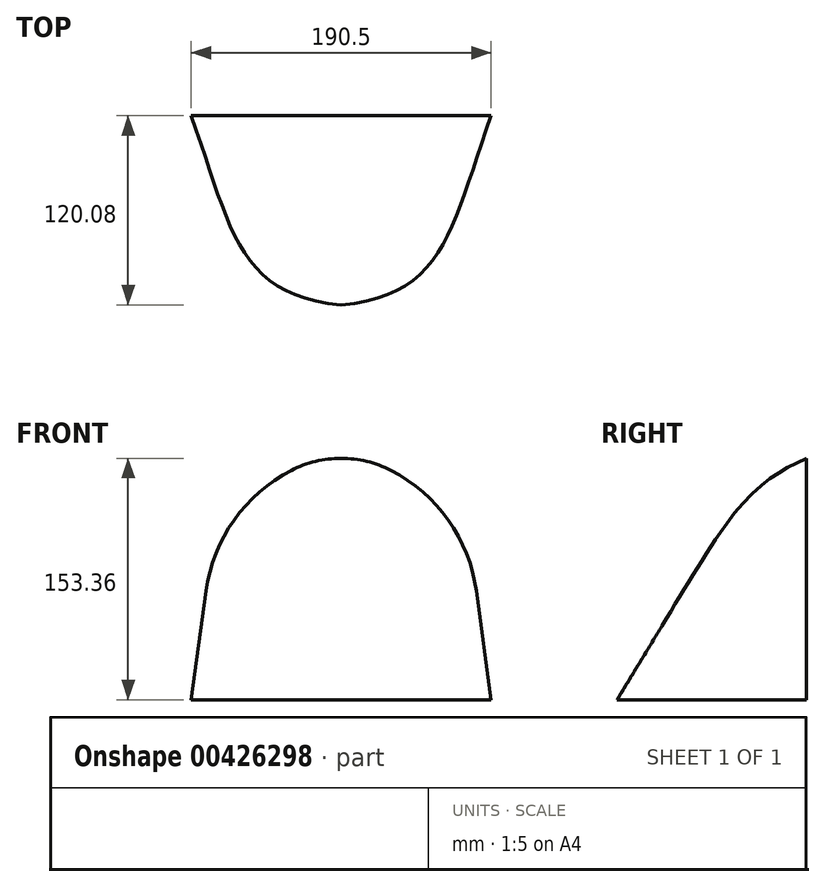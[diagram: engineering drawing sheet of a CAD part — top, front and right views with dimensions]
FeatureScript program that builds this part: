
annotation { "Feature Type Name" : "Feature", "Feature Type Description" : "" }
export const myFeature = defineFeature(function(context is Context, id is Id, definition is map)
    precondition{}
    {
        {
            var Q0;
            Q0=qCreatedBy(makeId("Front.planeOp"),FACE);
            var sketch = newSketch(context, id + "F0", { "sketchPlane" : qUnion([Q0])});
            skLineSegment(sketch, "E0", {"start": v(0, 111.3) * mm, "end": v(0, 0) * mm, "construction": true});
            skLineSegment(sketch, "E1", {"start": v(0, 0) * mm, "end": v(95.25, 0) * mm});
            skLineSegment(sketch, "E2", {"start": v(95.25, 0) * mm, "end": v(85.8, 69.13) * mm});
            skArc(sketch, "E3", {"start": v(85.8, 69.13) * mm, "mid": v(68.09, 114.03) * mm, "end": v(31.65, 145.7) * mm});
            skArc(sketch, "E4", {"start": v(31.65, 145.7) * mm, "mid": v(0, 153.36) * mm, "end": v(-31.65, 145.7) * mm});
            skArc(sketch, "E5.MirrorCS", {"start": v(-85.8, 69.13) * mm, "mid": v(-68.09, 114.03) * mm, "end": v(-31.65, 145.7) * mm});
            skLineSegment(sketch, "E6.MirrorCS", {"start": v(-95.25, 0) * mm, "end": v(-85.8, 69.13) * mm});
            skLineSegment(sketch, "E7.MirrorCS", {"start": v(0, 0) * mm, "end": v(-95.25, 0) * mm});
            skSolve(sketch);
        }
        {
            var Q0;
            Q0=qCreatedBy(makeId("Top.planeOp"),FACE);
            var sketch = newSketch(context, id + "F1", { "sketchPlane" : qUnion([Q0])});
            skLineSegment(sketch, "E8", {"start": v(-95.25, 0) * mm, "end": v(-70.05, -70.7) * mm, "construction": true});
            skArc(sketch, "E9", {"start": v(-70.05, -70.7) * mm, "mid": v(0, -120.08) * mm, "end": v(70.05, -70.7) * mm, "construction": true});
            skLineSegment(sketch, "E10", {"start": v(0, -4.05) * mm, "end": v(0, -115.34) * mm, "construction": true});
            skLineSegment(sketch, "E11", {"start": v(-95.25, 0) * mm, "end": v(95.25, 0) * mm});
            skLineSegment(sketch, "E12.MirrorCS", {"start": v(95.25, 0) * mm, "end": v(70.05, -70.7) * mm, "construction": true});
            skFitSpline(sketch, "E13", {"points": [v(0, -120.08) * mm, v(-95.25, 0) * mm], "startDerivative": vector(-198.66, 17.48) * mm, "endDerivative": vector(-75.61, 212.08) * mm});
            skFitSpline(sketch, "E14.MirrorCS", {"points": [v(0, -120.08) * mm, v(95.25, 0) * mm], "startDerivative": vector(198.66, 17.48) * mm, "endDerivative": vector(75.61, 212.08) * mm});
            skSolve(sketch);
        }
        {
            var Q0;
            Q0=qCreatedBy(makeId("Right.planeOp"),FACE);
            var sketch = newSketch(context, id + "F2", { "sketchPlane" : qUnion([Q0])});
            skArc(sketch, "E15", {"start": v(0, 153.36) * mm, "mid": v(-31.44, 134.53) * mm, "end": v(-55.27, 106.69) * mm, "construction": true});
            skLineSegment(sketch, "E16", {"start": v(-55.27, 106.69) * mm, "end": v(-120.08, 0) * mm, "construction": true});
            skFitSpline(sketch, "E17", {"points": [v(0, 153.36) * mm, v(-120.08, 0) * mm], "startDerivative": vector(-133.46, -61.2) * mm, "endDerivative": vector(-210.33, -343.88) * mm});
            skSolve(sketch);
        }
        {
            var Q0;
            Q0=makeQuery(id+"F0.imprint","IMPRINT",FACE,{"disambiguationData":[TD([[makeQuery(id+"F0.imprint","IMPRINT",EDGE,{"derivedFrom":sQuery(id+"F0.wireOp",EDGE,"E1")}),1.0]])]});
            var Q1;
            Q1=sQuery(id+"F2.wireOp",VERTEX,"E16.end");
            var Q2;
            Q2=sQuery(id+"F2.wireOp",EDGE,"E17");
            var Q3;
            Q3=sQuery(id+"F1.wireOp",EDGE,"E13");
            var Q4;
            Q4=sQuery(id+"F1.wireOp",EDGE,"E14.MirrorCS");
            loft(context, id + "F3", {"addGuides" : true, "sheetProfilesArray" : [{ "sheetProfileEntities" : qUnion([Q0]) }, { "sheetProfileEntities" : qUnion([Q1]) }], "guidesArray" : [{ "guideEntities" : qUnion([Q2]), "guideDerivativeType" : LoftGuideDerivativeType.DEFAULT, "guideDerivativeMagnitude" : 1 }, { "guideEntities" : qUnion([Q3]), "guideDerivativeType" : LoftGuideDerivativeType.DEFAULT, "guideDerivativeMagnitude" : 1 }, { "guideEntities" : qUnion([Q4]), "guideDerivativeType" : LoftGuideDerivativeType.DEFAULT, "guideDerivativeMagnitude" : 1 }]});
        }
    });
